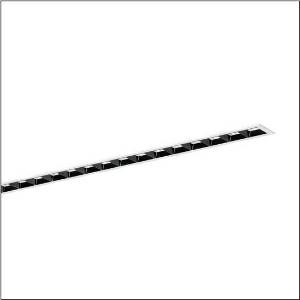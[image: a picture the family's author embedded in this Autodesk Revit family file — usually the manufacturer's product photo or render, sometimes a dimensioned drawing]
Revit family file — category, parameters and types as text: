
# Revit family: silica_r__21_51mx14tbt5w_b174
name_source: partatom
category: Lighting Fixtures
units: mm (PartAtom-declared; Revit-internal decimal feet)

## family parameters
Cut with Voids When Loaded = No
Host = Face
Light Source = No
Part Type = Normal
Room Calculation Point = No
Round Connector Dimension = Use Diameter
Shared = No

## types (1)
- --- (1 x LED, 4100 lm, 40.5 W, 6500K)
    Apparent Load = 41 VA
    CIE Flux Codes = 74 94 99 100 100
    Color Rendering = 80
    Color Temperature = 6500K
    Default Elevation = 1800 mm
    Description = Silica® 21, office luminaire, primary light control with darklight reflector, of PMMA, black, light emission: direct distribution, primary light characteristic: asymmetric, installation type: recessed, LED, rated luminous flux: 4.100lm, luminous efficacy: 96lm/W, light colour: 8tw, colour temperature: 2700..6500K, with terminal, 3+2-pole, max. 2.5mm², mains connection: 220..240V, AC, 50/60Hz, rated input power: 42.6W, luminaire housing, of aluminium, traffic white (RAL 9016), length: 1.528mm, width: 79mm, height: 53mm, protection rating (complete): IP20, insulation class (complete): insulation class I (protective earthing), certification: CE, permissible operating ambient temperature: 0..+35°C, standard: EN 50419, packaging unit: 1 piece
    Height = 0 mm  [stored 0 ft]
    Lamp = 1 x LED
    Lamp Light Flux = 4100 lm
    Lamp Power = 40.5 W
    Lamp count = 1
    Length = 1527 mm
    Luminous efficacy = 101 lm/W
    Manufacturer = Siteco
    ModVariant = No
    Model = 51MX14TBT5W
    Mounting Place = Ceiling
    Mounting Type = Recessed
    Number of Poles = 1
    OnlyDefault = Yes
    Power Factor = 1
    Product Name = Silica® 21
    Product group = office luminaire | ceiling recessed
    ProductGroupID = 400
    Protection Class = Protection class I
    Protection Degree = IP 20
    RLX_Detail_Level = 1
    RlxData = <blob elided: 39537 chars, md5=0ca806e0>
    Socket = socket
    Standby Power = 0 W
    System Light Flux = 4100 lm
    System Power = 41 W
    Type Comments = individual setting
    Type Image = l_1251632.jpg
    URL = http://relux.com
    VarID = @adj_046119
    Voltage = 0 V
    Weight = 0.00 kg
    Width = 79 mm

note: [stored X ft] marks values corroborated as IEEE doubles in the binary element streams (Revit-internal decimal feet)

## geometry (parser evidence)
native form markers: Blend x4, Sweep x10
no freeform markers — native parametric forms only
